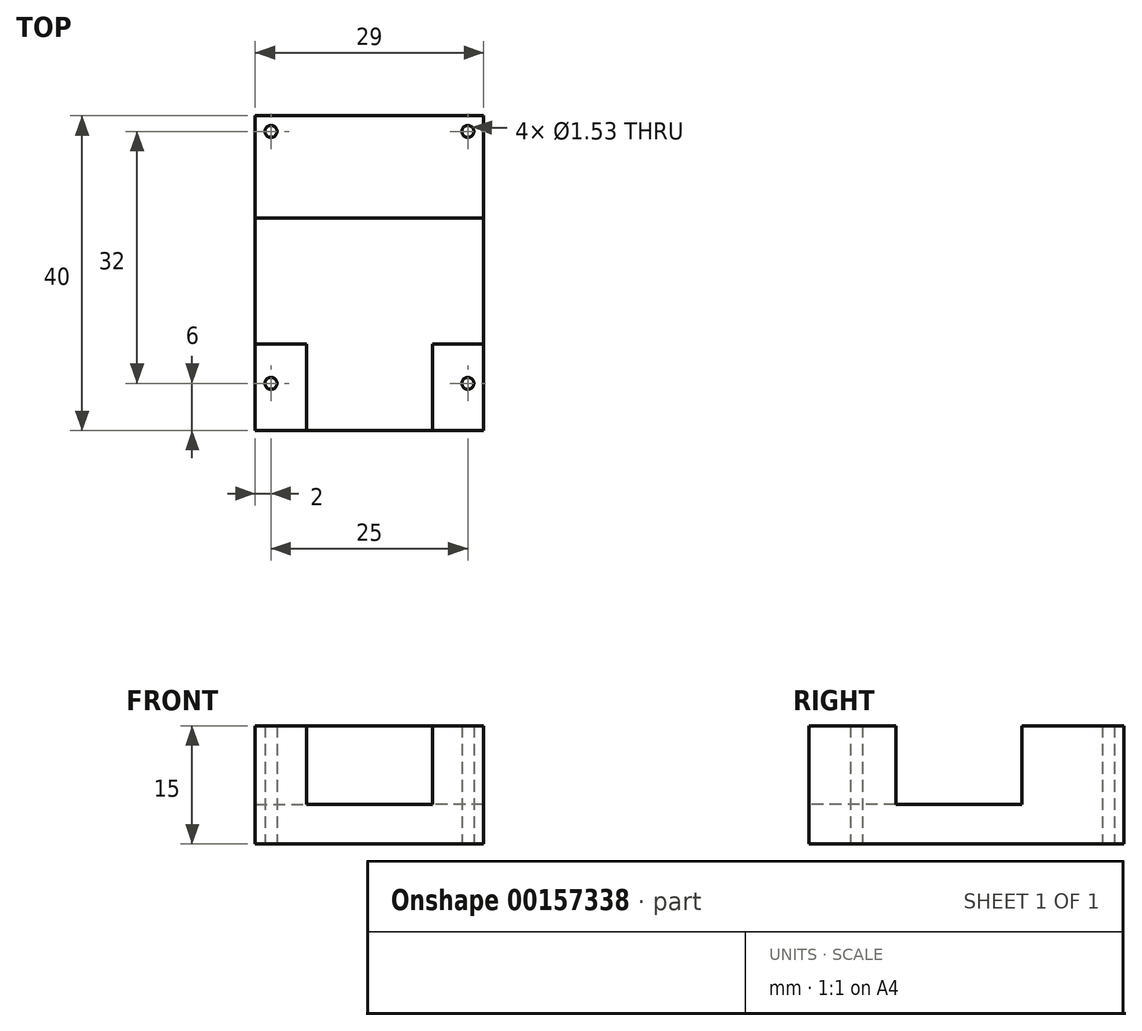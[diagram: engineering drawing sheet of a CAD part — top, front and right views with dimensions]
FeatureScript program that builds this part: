
annotation { "Feature Type Name" : "Feature", "Feature Type Description" : "" }
export const myFeature = defineFeature(function(context is Context, id is Id, definition is map)
    precondition{}
    {
        {
            var Q0;
            Q0=qCreatedBy(makeId("Top.planeOp"),FACE);
            var sketch = newSketch(context, id + "F0", { "sketchPlane" : qUnion([Q0])});
            skLineSegment(sketch, "E0.bottom", {"start": v(14.5, 20) * mm, "end": v(-14.5, 20) * mm});
            skLineSegment(sketch, "E0.top", {"start": v(14.5, -20) * mm, "end": v(-14.5, -20) * mm});
            skLineSegment(sketch, "E0.left", {"start": v(14.5, 20) * mm, "end": v(14.5, -20) * mm});
            skLineSegment(sketch, "E0.right", {"start": v(-14.5, 20) * mm, "end": v(-14.5, -20) * mm});
            skPoint(sketch, "E0.middle", {"position": v(0, 0) * mm});
            skCircle(sketch, "E1", {"center": v(-12.5, 18) * mm, "radius": 0.77 * mm});
            skCircle(sketch, "E2", {"center": v(12.5, 18) * mm, "radius": 0.77 * mm});
            skCircle(sketch, "E3", {"center": v(12.5, -14) * mm, "radius": 0.77 * mm});
            skCircle(sketch, "E4", {"center": v(-12.5, -14) * mm, "radius": 0.77 * mm});
            skSolve(sketch);
        }
        {
            var Q0;
            Q0=makeQuery(id+"F0.imprint","IMPRINT",FACE,{"disambiguationData":[TD([[makeQuery(id+"F0.imprint","IMPRINT",EDGE,{"derivedFrom":sQuery(id+"F0.wireOp",EDGE,"E0.bottom")}),1.0]])]});
            extrude(context, id + "F1", {"entities" : qUnion([Q0]), "depth" : 15 * mm});
        }
        {
            var Q0;
            Q0=makeQuery(id+"F1.opExtrude","CAP_FACE",FACE,{"disambiguationData":[OSD([sQuery(id+"F0.wireOp",EDGE,"E0.bottom"),sQuery(id+"F0.wireOp",EDGE,"E0.top"),sQuery(id+"F0.wireOp",EDGE,"E0.left"),sQuery(id+"F0.wireOp",EDGE,"E0.right"),sQuery(id+"F0.wireOp",EDGE,"E1"),sQuery(id+"F0.wireOp",EDGE,"E2"),sQuery(id+"F0.wireOp",EDGE,"E3"),sQuery(id+"F0.wireOp",EDGE,"E4")])],"isStart":false});
            var sketch = newSketch(context, id + "F2", { "sketchPlane" : qUnion([Q0])});
            skLineSegment(sketch, "E5.0.0", {"start": v(-14.5, -20) * mm, "end": v(14.5, -20) * mm});
            skLineSegment(sketch, "E5.0.1", {"start": v(14.5, -20) * mm, "end": v(14.5, 20) * mm});
            skLineSegment(sketch, "E5.0.2", {"start": v(14.5, 20) * mm, "end": v(-14.5, 20) * mm});
            skLineSegment(sketch, "E5.0.3", {"start": v(-14.5, 20) * mm, "end": v(-14.5, -20) * mm});
            skLineSegment(sketch, "E6", {"start": v(-14.5, 7) * mm, "end": v(14.5, 7) * mm});
            skLineSegment(sketch, "E7", {"start": v(14.5, 7) * mm, "end": v(14.5, -9) * mm});
            skLineSegment(sketch, "E8", {"start": v(14.5, -9) * mm, "end": v(-14.5, -9) * mm});
            skPoint(sketch, "E9", {"position": v(-12.5, 18) * mm});
            skPoint(sketch, "E10", {"position": v(-12.5, -14) * mm});
            skSolve(sketch);
        }
        {
            var Q0;
            {var subQ0=sQuery(id+"F2.wireOp",EDGE,"E6");Q0=makeQuery(id+"F2.imprint","IMPRINT",FACE,{"disambiguationData":[TD([[makeQuery(id+"F2.imprint","IMPRINT",EDGE,{"derivedFrom":subQ0}),-1.0]])]});}
            extrude(context, id + "F3", {"entities" : qUnion([Q0]), "operationType" : NewBodyOperationType.REMOVE, "oppositeDirection" : true, "depth" : 10 * mm});
        }
        {
            var Q0;
            Q0=makeQuery(id+"F1.opExtrude","SWEPT_FACE",FACE,{"disambiguationData":[OSD([sQuery(id+"F0.wireOp",EDGE,"E0.top")])]});
            var sketch = newSketch(context, id + "F4", { "sketchPlane" : qUnion([Q0])});
            skLineSegment(sketch, "E11.0.0", {"start": v(-14.5, 0) * mm, "end": v(14.5, 0) * mm});
            skLineSegment(sketch, "E11.0.1", {"start": v(14.5, 0) * mm, "end": v(14.5, 15) * mm});
            skLineSegment(sketch, "E11.0.2", {"start": v(14.5, 15) * mm, "end": v(-14.5, 15) * mm});
            skLineSegment(sketch, "E11.0.3", {"start": v(-14.5, 15) * mm, "end": v(-14.5, 0) * mm});
            skLineSegment(sketch, "E12.bottom", {"start": v(8, 25) * mm, "end": v(-8, 25) * mm});
            skLineSegment(sketch, "E12.top", {"start": v(8, 5) * mm, "end": v(-8, 5) * mm});
            skLineSegment(sketch, "E12.left", {"start": v(8, 25) * mm, "end": v(8, 5) * mm});
            skLineSegment(sketch, "E12.right", {"start": v(-8, 25) * mm, "end": v(-8, 5) * mm});
            skPoint(sketch, "E12.middle", {"position": v(0, 15) * mm});
            skSolve(sketch);
        }
        {
            var Q0;
            {var subQ5=sQuery(id+"F4.wireOp",EDGE,"E12.top");Q0=makeQuery(id+"F4.imprint","IMPRINT",FACE,{"disambiguationData":[TD([[makeQuery(id+"F4.imprint","IMPRINT",EDGE,{"derivedFrom":subQ5}),-1.0]])]});}
            extrude(context, id + "F5", {"entities" : qUnion([Q0]), "operationType" : NewBodyOperationType.REMOVE, "oppositeDirection" : true, "depth" : 25 * mm});
        }
    });
